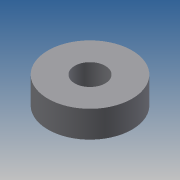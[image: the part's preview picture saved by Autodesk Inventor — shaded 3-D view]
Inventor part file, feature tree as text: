
AUTODESK INVENTOR PART (.ipt)
format: ipt  version: 2013 (Build 170138000, 138)  size: 72,192 bytes
history: native  units: mm
features: extrude x1, sketch x1
ambient origin geometry x8: Origin, YZ Plane, XZ Plane, XY Plane, X Axis, Y Axis, Z Axis, Center Point
bodies: Solid1 (feature_tree)
feature tree (2):
  extrude  "Extrusion1"  Depth=22.0mm
  sketch  "Sketch1"  dims[d0=8.0mm d2=22.0mm d3=7.0mm d4=0.0mm]
